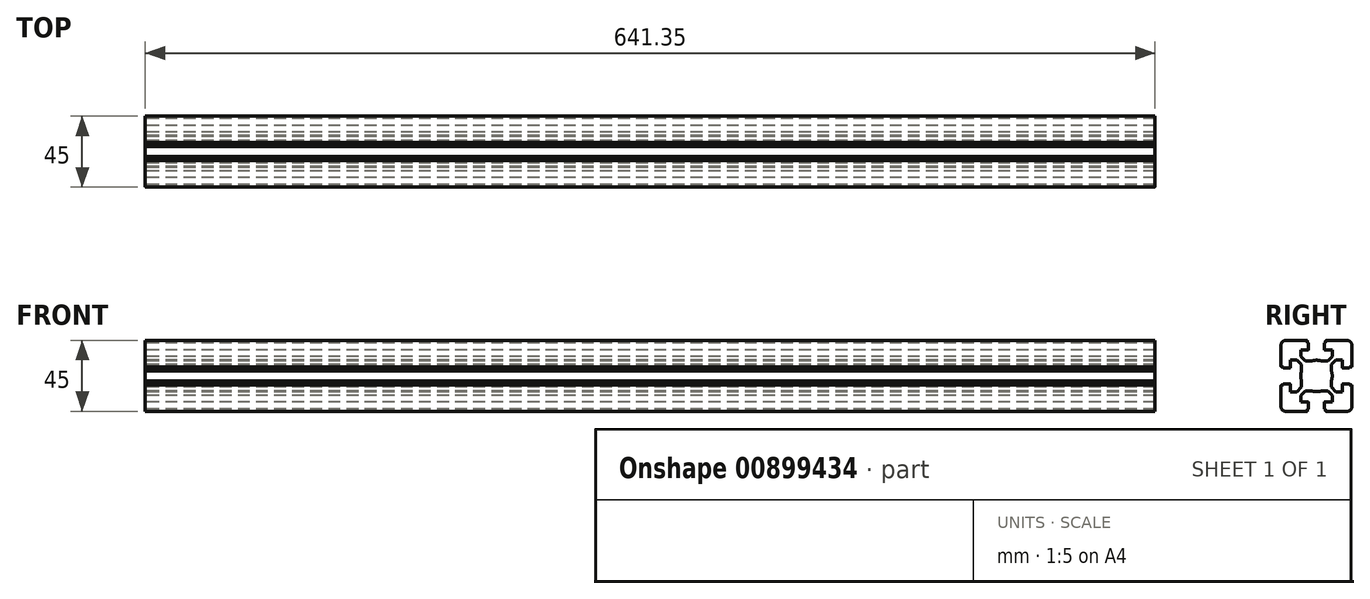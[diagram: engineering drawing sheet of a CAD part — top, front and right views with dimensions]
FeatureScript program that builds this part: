
annotation { "Feature Type Name" : "Feature", "Feature Type Description" : "" }
export const myFeature = defineFeature(function(context is Context, id is Id, definition is map)
    precondition{}
    {
        {
            var Q0;
            Q0=qCreatedBy(makeId("Right.planeOp"),FACE);
            var sketch = newSketch(context, id + "F0", { "sketchPlane" : qUnion([Q0])});
            skLineSegment(sketch, "E0", {"start": v(-20.09, -10.29) * mm, "end": v(-21.29, -10.29) * mm});
            skArc(sketch, "E1", {"start": v(-21.29, -10.29) * mm, "mid": v(-21.5, -10.38) * mm, "end": v(-21.59, -10.59) * mm});
            skLineSegment(sketch, "E2", {"start": v(-21.59, -10.59) * mm, "end": v(-21.59, -23.99) * mm});
            skArc(sketch, "E3", {"start": v(-21.59, -23.99) * mm, "mid": v(-20.7, -26.11) * mm, "end": v(-18.59, -26.99) * mm});
            skLineSegment(sketch, "E4", {"start": v(-18.59, -26.99) * mm, "end": v(-5.19, -26.99) * mm});
            skArc(sketch, "E5", {"start": v(-5.19, -26.99) * mm, "mid": v(-4.98, -26.9) * mm, "end": v(-4.89, -26.69) * mm});
            skLineSegment(sketch, "E6", {"start": v(-4.89, -26.69) * mm, "end": v(-4.89, -25.49) * mm});
            skLineSegment(sketch, "E7", {"start": v(-4.89, -25.49) * mm, "end": v(-4.39, -25.49) * mm});
            skArc(sketch, "E8", {"start": v(-4.39, -25.49) * mm, "mid": v(-4.18, -25.4) * mm, "end": v(-4.09, -25.19) * mm});
            skLineSegment(sketch, "E9", {"start": v(-4.09, -25.19) * mm, "end": v(-4.09, -21.29) * mm});
            skArc(sketch, "E10", {"start": v(-4.09, -21.29) * mm, "mid": v(-4.18, -21.08) * mm, "end": v(-4.39, -20.99) * mm});
            skLineSegment(sketch, "E11", {"start": v(-4.39, -20.99) * mm, "end": v(-9.14, -20.99) * mm});
            skLineSegment(sketch, "E12", {"start": v(-9.14, -20.99) * mm, "end": v(-9.14, -16.88) * mm});
            skLineSegment(sketch, "E13", {"start": v(-9.14, -16.88) * mm, "end": v(-6.25, -13.99) * mm});
            skLineSegment(sketch, "E14", {"start": v(-6.25, -13.99) * mm, "end": v(-2.21, -13.99) * mm});
            skArc(sketch, "E15", {"start": v(-2.21, -13.99) * mm, "mid": v(0.91, -14.49) * mm, "end": v(4.03, -13.99) * mm});
            skLineSegment(sketch, "E16", {"start": v(-20.09, -10.29) * mm, "end": v(-20.09, -9.79) * mm});
            skArc(sketch, "E17", {"start": v(-20.09, -9.79) * mm, "mid": v(-20, -9.58) * mm, "end": v(-19.79, -9.49) * mm});
            skLineSegment(sketch, "E18", {"start": v(-19.79, -9.49) * mm, "end": v(-15.89, -9.49) * mm});
            skArc(sketch, "E19", {"start": v(-15.89, -9.49) * mm, "mid": v(-15.68, -9.58) * mm, "end": v(-15.59, -9.79) * mm});
            skLineSegment(sketch, "E20", {"start": v(-15.59, -9.79) * mm, "end": v(-15.59, -14.54) * mm});
            skLineSegment(sketch, "E21", {"start": v(-15.59, -14.54) * mm, "end": v(-11.48, -14.54) * mm});
            skLineSegment(sketch, "E22", {"start": v(-11.48, -14.54) * mm, "end": v(-8.59, -11.65) * mm});
            skLineSegment(sketch, "E23", {"start": v(-8.59, -11.65) * mm, "end": v(-8.59, -7.61) * mm});
            skLineSegment(sketch, "E24", {"start": v(29.82, -4.49) * mm, "end": v(-31.05, -4.49) * mm});
            skLineSegment(sketch, "E25.MirrorCS", {"start": v(6.71, -25.49) * mm, "end": v(6.21, -25.49) * mm});
            skArc(sketch, "E26.MirrorCS", {"start": v(7.01, -26.99) * mm, "mid": v(6.8, -26.9) * mm, "end": v(6.71, -26.69) * mm});
            skLineSegment(sketch, "E27.MirrorCS", {"start": v(10.41, -11.65) * mm, "end": v(10.41, -7.61) * mm});
            skArc(sketch, "E28.MirrorCS", {"start": v(6.21, -25.49) * mm, "mid": v(6, -25.4) * mm, "end": v(5.91, -25.19) * mm});
            skLineSegment(sketch, "E29.MirrorCS", {"start": v(6.71, -26.69) * mm, "end": v(6.71, -25.49) * mm});
            skArc(sketch, "E30.MirrorCS", {"start": v(5.91, -21.29) * mm, "mid": v(6, -21.08) * mm, "end": v(6.21, -20.99) * mm});
            skLineSegment(sketch, "E31.MirrorCS", {"start": v(10.96, -16.88) * mm, "end": v(8.07, -13.99) * mm});
            skLineSegment(sketch, "E32.MirrorCS", {"start": v(13.3, -14.54) * mm, "end": v(10.41, -11.65) * mm});
            skLineSegment(sketch, "E33.MirrorCS", {"start": v(17.41, -14.54) * mm, "end": v(13.3, -14.54) * mm});
            skLineSegment(sketch, "E34.MirrorCS", {"start": v(17.41, -9.79) * mm, "end": v(17.41, -14.54) * mm});
            skLineSegment(sketch, "E35.MirrorCS", {"start": v(6.21, -20.99) * mm, "end": v(10.96, -20.99) * mm});
            skLineSegment(sketch, "E36.MirrorCS", {"start": v(8.07, -13.99) * mm, "end": v(4.03, -13.99) * mm});
            skArc(sketch, "E37.MirrorCS", {"start": v(4.03, -13.99) * mm, "mid": v(0.91, -14.49) * mm, "end": v(-2.21, -13.99) * mm});
            skLineSegment(sketch, "E38.MirrorCS", {"start": v(10.96, -20.99) * mm, "end": v(10.96, -16.88) * mm});
            skLineSegment(sketch, "E39.MirrorCS", {"start": v(5.91, -25.19) * mm, "end": v(5.91, -21.29) * mm});
            skArc(sketch, "E40.MirrorCS", {"start": v(23.41, -23.99) * mm, "mid": v(22.53, -26.11) * mm, "end": v(20.41, -26.99) * mm});
            skLineSegment(sketch, "E41.MirrorCS", {"start": v(20.41, -26.99) * mm, "end": v(7.01, -26.99) * mm});
            skLineSegment(sketch, "E42.MirrorCS", {"start": v(23.41, -10.59) * mm, "end": v(23.41, -23.99) * mm});
            skArc(sketch, "E43.MirrorCS", {"start": v(17.71, -9.49) * mm, "mid": v(17.5, -9.58) * mm, "end": v(17.41, -9.79) * mm});
            skArc(sketch, "E44.MirrorCS", {"start": v(23.11, -10.29) * mm, "mid": v(23.32, -10.38) * mm, "end": v(23.41, -10.59) * mm});
            skLineSegment(sketch, "E45.MirrorCS", {"start": v(21.91, -10.29) * mm, "end": v(21.91, -9.79) * mm});
            skLineSegment(sketch, "E46.MirrorCS", {"start": v(21.91, -10.29) * mm, "end": v(23.11, -10.29) * mm});
            skArc(sketch, "E47.MirrorCS", {"start": v(21.91, -9.79) * mm, "mid": v(21.82, -9.58) * mm, "end": v(21.61, -9.49) * mm});
            skLineSegment(sketch, "E48.MirrorCS", {"start": v(21.61, -9.49) * mm, "end": v(17.71, -9.49) * mm});
            skLineSegment(sketch, "E49.MirrorCS", {"start": v(6.71, 16.51) * mm, "end": v(6.21, 16.51) * mm});
            skArc(sketch, "E50.MirrorCS", {"start": v(-4.39, 16.51) * mm, "mid": v(-4.18, 16.42) * mm, "end": v(-4.09, 16.21) * mm});
            skLineSegment(sketch, "E51.MirrorCS", {"start": v(-4.89, 16.51) * mm, "end": v(-4.39, 16.51) * mm});
            skArc(sketch, "E52.MirrorCS", {"start": v(5.91, 12.31) * mm, "mid": v(6, 12.1) * mm, "end": v(6.21, 12.01) * mm});
            skLineSegment(sketch, "E53.MirrorCS", {"start": v(6.71, 17.71) * mm, "end": v(6.71, 16.51) * mm});
            skLineSegment(sketch, "E54.MirrorCS", {"start": v(-4.89, 17.71) * mm, "end": v(-4.89, 16.51) * mm});
            skArc(sketch, "E55.MirrorCS", {"start": v(-5.19, 18.01) * mm, "mid": v(-4.98, 17.92) * mm, "end": v(-4.89, 17.71) * mm});
            skArc(sketch, "E56.MirrorCS", {"start": v(-4.09, 12.31) * mm, "mid": v(-4.18, 12.1) * mm, "end": v(-4.39, 12.01) * mm});
            skArc(sketch, "E57.MirrorCS", {"start": v(7.01, 18.01) * mm, "mid": v(6.8, 17.92) * mm, "end": v(6.71, 17.71) * mm});
            skArc(sketch, "E58.MirrorCS", {"start": v(6.21, 16.51) * mm, "mid": v(6, 16.42) * mm, "end": v(5.91, 16.21) * mm});
            skArc(sketch, "E59.MirrorCS", {"start": v(23.11, 1.31) * mm, "mid": v(23.32, 1.4) * mm, "end": v(23.41, 1.61) * mm});
            skLineSegment(sketch, "E60.MirrorCS", {"start": v(21.91, 1.31) * mm, "end": v(21.91, 0.81) * mm});
            skArc(sketch, "E61.MirrorCS", {"start": v(-15.89, 0.51) * mm, "mid": v(-15.68, 0.6) * mm, "end": v(-15.59, 0.81) * mm});
            skArc(sketch, "E62.MirrorCS", {"start": v(-21.29, 1.31) * mm, "mid": v(-21.5, 1.4) * mm, "end": v(-21.59, 1.61) * mm});
            skArc(sketch, "E63.MirrorCS", {"start": v(17.71, 0.51) * mm, "mid": v(17.5, 0.6) * mm, "end": v(17.41, 0.81) * mm});
            skArc(sketch, "E64.MirrorCS", {"start": v(21.91, 0.81) * mm, "mid": v(21.82, 0.6) * mm, "end": v(21.61, 0.51) * mm});
            skLineSegment(sketch, "E65.MirrorCS", {"start": v(21.91, 1.31) * mm, "end": v(23.11, 1.31) * mm});
            skArc(sketch, "E66.MirrorCS", {"start": v(14.31, 5.31) * mm, "mid": v(14.1, 5.4) * mm, "end": v(14.01, 5.61) * mm});
            skArc(sketch, "E67.MirrorCS", {"start": v(-20.09, 0.81) * mm, "mid": v(-20, 0.6) * mm, "end": v(-19.79, 0.51) * mm});
            skLineSegment(sketch, "E68.MirrorCS", {"start": v(-20.09, 1.31) * mm, "end": v(-21.29, 1.31) * mm});
            skLineSegment(sketch, "E69.MirrorCS", {"start": v(-20.09, 1.31) * mm, "end": v(-20.09, 0.81) * mm});
            skLineSegment(sketch, "E70.MirrorCS", {"start": v(8.07, 5.01) * mm, "end": v(4.03, 5.01) * mm});
            skLineSegment(sketch, "E71.MirrorCS", {"start": v(-4.09, 16.21) * mm, "end": v(-4.09, 12.31) * mm});
            skLineSegment(sketch, "E72.MirrorCS", {"start": v(-9.14, 12.01) * mm, "end": v(-9.14, 7.9) * mm});
            skLineSegment(sketch, "E73.MirrorCS", {"start": v(-15.59, 5.56) * mm, "end": v(-11.48, 5.56) * mm});
            skLineSegment(sketch, "E74.MirrorCS", {"start": v(-4.39, 12.01) * mm, "end": v(-9.14, 12.01) * mm});
            skLineSegment(sketch, "E75.MirrorCS", {"start": v(-9.14, 7.9) * mm, "end": v(-6.25, 5.01) * mm});
            skLineSegment(sketch, "E76.MirrorCS", {"start": v(10.96, 12.01) * mm, "end": v(10.96, 7.9) * mm});
            skArc(sketch, "E77.MirrorCS", {"start": v(-21.59, 15.01) * mm, "mid": v(-20.7, 17.13) * mm, "end": v(-18.59, 18.01) * mm});
            skLineSegment(sketch, "E78.MirrorCS", {"start": v(23.41, 1.61) * mm, "end": v(23.41, 15.01) * mm});
            skLineSegment(sketch, "E79.MirrorCS", {"start": v(13.3, 5.56) * mm, "end": v(10.41, 2.67) * mm});
            skLineSegment(sketch, "E80.MirrorCS", {"start": v(-8.59, 2.67) * mm, "end": v(-8.59, -1.37) * mm});
            skLineSegment(sketch, "E81.MirrorCS", {"start": v(-15.59, 0.81) * mm, "end": v(-15.59, 5.56) * mm});
            skLineSegment(sketch, "E82.MirrorCS", {"start": v(10.41, 2.67) * mm, "end": v(10.41, -1.37) * mm});
            skLineSegment(sketch, "E83.MirrorCS", {"start": v(-18.59, 18.01) * mm, "end": v(-5.19, 18.01) * mm});
            skLineSegment(sketch, "E84.MirrorCS", {"start": v(10.96, 7.9) * mm, "end": v(8.07, 5.01) * mm});
            skLineSegment(sketch, "E85.MirrorCS", {"start": v(17.41, 5.56) * mm, "end": v(13.3, 5.56) * mm});
            skArc(sketch, "E86.MirrorCS", {"start": v(23.41, 15.01) * mm, "mid": v(22.53, 17.13) * mm, "end": v(20.41, 18.01) * mm});
            skLineSegment(sketch, "E87.MirrorCS", {"start": v(5.91, 16.21) * mm, "end": v(5.91, 12.31) * mm});
            skLineSegment(sketch, "E88.MirrorCS", {"start": v(17.41, 0.81) * mm, "end": v(17.41, 5.56) * mm});
            skLineSegment(sketch, "E89.MirrorCS", {"start": v(-11.48, 5.56) * mm, "end": v(-8.59, 2.67) * mm});
            skLineSegment(sketch, "E90.MirrorCS", {"start": v(-6.25, 5.01) * mm, "end": v(-2.21, 5.01) * mm});
            skLineSegment(sketch, "E91.MirrorCS", {"start": v(-21.59, 1.61) * mm, "end": v(-21.59, 15.01) * mm});
            skArc(sketch, "E92.MirrorCS", {"start": v(4.03, 5.01) * mm, "mid": v(0.91, 5.51) * mm, "end": v(-2.21, 5.01) * mm});
            skLineSegment(sketch, "E93.MirrorCS", {"start": v(6.21, 12.01) * mm, "end": v(10.96, 12.01) * mm});
            skArc(sketch, "E94.MirrorCS", {"start": v(-2.21, 5.01) * mm, "mid": v(0.91, 5.51) * mm, "end": v(4.03, 5.01) * mm});
            skLineSegment(sketch, "E95.MirrorCS", {"start": v(20.41, 18.01) * mm, "end": v(7.01, 18.01) * mm});
            skLineSegment(sketch, "E96.MirrorCS", {"start": v(-19.79, 0.51) * mm, "end": v(-15.89, 0.51) * mm});
            skLineSegment(sketch, "E97.MirrorCS", {"start": v(21.61, 0.51) * mm, "end": v(17.71, 0.51) * mm});
            skLineSegment(sketch, "E98.MirrorCS", {"start": v(0.91, -27.65) * mm, "end": v(0.91, 19.82) * mm});
            skArc(sketch, "E99", {"start": v(-8.59, -1.37) * mm, "mid": v(-9.09, -4.49) * mm, "end": v(-8.59, -7.61) * mm});
            skArc(sketch, "E100", {"start": v(10.41, -7.61) * mm, "mid": v(10.91, -4.49) * mm, "end": v(10.41, -1.37) * mm});
            skSolve(sketch);
        }
        {
            var Q0;
            Q0=qSketchRegion(id+"F0",true);
            extrude(context, id + "F1", {"entities" : qUnion([Q0]), "depth" : 641.35 * mm, "offsetDistance" : 25.4 * mm});
        }
    });
